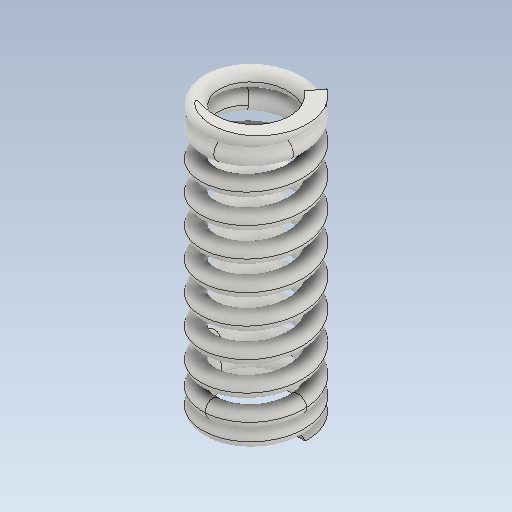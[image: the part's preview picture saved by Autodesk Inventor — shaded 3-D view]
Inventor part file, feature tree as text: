
AUTODESK INVENTOR PART (.ipt)
format: ipt  version: 2020 (Build 240168000, 168)  size: 1,127,424 bytes
history: native  units: mm
features: other x67, extrude x8, helix x5, sketch x3, sweep x2, plane x1
ambient origin geometry x8: Origin, YZ Plane, XZ Plane, XY Plane, X Axis, Y Axis, Z Axis, Center Point
bodies: Solid1 (feature_tree)
feature tree (86):
  other  "Main Coil Path(Right)"
  other  "Section Work Plane(Right)"
  other  "Start Work Plane(Right)"
  other  "End Work Plane(Right)"
  other  "End Cut Work Plane(Right)"
  other  "Start Cut Work Plane(Right)"
  other  "Plain Ends Cut Work Plane 1(Right)"
  other  "Plain Ends Cut Work Plane 2(Right)"
  sweep  "Main Coil Feature(R)"
  other  "Start Transition Coil 1(Right)"
  helix  "Coil  Start Transition 2(R)"  [1 undecoded]
  helix  "Coil  Start Transition 3(R)"  [1 undecoded]
  helix  "Coil  Start Transition 4(R)"  [1 undecoded]
  other  "Start Ends Coil(Right)"
  extrude  "Start Cut Feature(Right)"  Depth=10.0mm
  other  "End Transition Coil 1(Right)"
  other  "End Transition Coil 2(Right)"
  other  "End Transition Coil 3(Right)"
  other  "End Transition Coil 4(Right)"
  other  "End Coil(Right)"
  extrude  "End Cut Feature(Right)"  Depth=10.0mm
  extrude  "Plain Ends Cut Feature 1(Right)"  Depth=10.0mm
  extrude  "Plain Ends Cut  2(R)"  Depth=10.0mm TaperAngle=0.0deg
  other  "Main Coil Path(Left)"
  other  "Section Work Plane(Left)"
  other  "Start Work Plane(Left)"
  other  "End Work Plane(Left)"
  other  "End Cut Work Plane(Left)"
  other  "Start Cut Work Plane(Left)"
  other  "Plain Ends Cut Work Plane 1(Left)"
  other  "Plain Ends Cut Work Plane 2(Left)"
  sweep  "Main Coil Feature(L)"
  other  "Start Transition Coil 1(Left)"
  other  "Start Transition Coil 2(Left)"
  other  "Start Transition Coil 3(Left)"
  other  "Start Transition Coil 4(Left)"
  other  "Start Ends Coil(Left)"
  extrude  "Start Cut Feature(Left)"  Depth=10.0mm TaperAngle=0.0deg
  other  "End Transition Coil 1(Left)"
  other  "End Transition Coil 2(Left)"
  other  "End Transition Coil 3(Left)"
  other  "End Transition Coil 4(Left)"
  other  "End Coil(Left)"
  extrude  "End Cut Feature(Left)"  Depth=10.0mm
  extrude  "Cut Plain Ends Cut 1(L)"  TaperAngle=0.0deg  [1 undecoded]
  extrude  "Cut Plain Ends Cut 2(L)"  TaperAngle=0.0deg  [1 undecoded]
  other  "iMate Based Work Plane"
  other  "Preview Center Point"
  other  "Preview X Axis"
  other  "Path Section Sketch(Right)"
  other  "Srf1"
  helix  "Coil Section Sketch(Right)"  [1 undecoded]
  other  "Start Transition Coil Sketch 1(Right)"
  sketch  "Sketch  Start Transition 2(R)"  dims[d0=0.3mm d2=2.11556mm d3=10.0mm d4=69.0mm]
  sketch  "Sketch  Start Transition 3(R)"  dims[d5=0.0mm d6=90.0deg d7=90.0deg d8=0.0mm d9=0.0mm d12=2.357522mm d13=-3.04512mm d14=1.2mm]
  sketch  "Sketch  Start Transition 4(R)"  dims[d15=0.0mm d16=1.88667mm d17=10.0mm d18=2.5mm d19=0.0mm d20=90.0deg d21=90.0deg d22=0.0mm d23=0.0mm d24=1.65778mm d25=10.0mm d26=2.5mm d27=0.0mm d28=90.0deg d29=90.0deg d30=0.0mm d31=0.0mm d32=1.42889mm d33=10.0mm d34=2.5mm d35=0.0mm d36=90.0deg d37=90.0deg d38=0.0mm d39=0.0mm d40=1.2mm d41=10.0mm d42=2.5mm d43=0.0mm d44=90.0deg d45=90.0deg d46=0.0mm d47=0.0mm d48=1.88667mm d49=10.0mm d50=1.875mm d51=0.0mm d52=90.0deg d53=90.0deg d54=0.0mm d55=0.0mm d56=1.65778mm d57=10.0mm d58=1.875mm d59=0.0mm d60=90.0deg d61=90.0deg d62=0.0mm d63=0.0mm d64=1.42889mm d65=10.0mm d66=1.875mm d67=0.0mm d68=90.0deg d69=90.0deg d70=0.0mm d71=0.0mm d72=1.2mm d73=10.0mm d74=1.875mm d75=0.0mm d76=90.0deg d77=90.0deg d78=0.0mm d79=0.0mm d81=10.0mm d82=15.0mm d83=0.0mm d84=90.0deg d85=90.0deg d86=0.0mm d87=0.0mm d88=1.207057mm d89=10.0mm d90=10.0mm d91=0.0mm d92=90.0deg d93=90.0deg d94=0.0mm d95=0.0mm d96=7.4mm d97=1.207057mm d98=0.0mm d99=7.4mm d100=1.207057mm d101=0.0mm d102=0.0mm d103=0.0mm d104=0.0mm d105=0.0mm d106=0.0mm d108=0.0mm d112=0.0mm d113=0.0mm d114=0.0mm d121=0.308801mm d131=0.0mm d132=0.0mm d133=0.0mm d134=0.0mm d135=0.3mm d137=2.11556mm d138=10.0mm d139=69.0mm d140=0.0mm d141=90.0deg d142=90.0deg d143=0.0mm d144=0.0mm d145=2.357522mm d146=-3.04512mm d147=0.308801mm d148=0.007037mm d149=1.2mm d150=0.0mm d151=0.0mm d152=1.88667mm d153=10.0mm d154=2.5mm d155=0.0mm d156=90.0deg d157=90.0deg d158=0.0mm d159=0.0mm d160=1.65778mm d161=10.0mm d162=2.5mm d163=0.0mm d164=90.0deg d165=90.0deg d166=0.0mm d167=0.0mm d168=1.42889mm d169=10.0mm d170=2.5mm d171=0.0mm d172=90.0deg d173=90.0deg d174=0.0mm d175=0.0mm d176=1.2mm d177=10.0mm d178=2.5mm d179=0.0mm d180=90.0deg d181=90.0deg d182=0.0mm d183=0.0mm d184=10.0mm d185=10.0mm d186=10.0mm d187=10.0mm d188=1.207057mm d189=10.0mm d190=15.0mm d191=0.0mm d192=90.0deg d193=90.0deg d194=0.0mm d195=0.0mm d196=10.0mm d197=7.4mm d198=1.207057mm d199=0.0mm d200=10.0mm d201=1.88667mm d202=10.0mm d203=1.875mm d204=0.0mm d205=90.0deg d206=90.0deg d207=0.0mm d208=0.0mm d209=10.0mm d210=1.65778mm d211=10.0mm d212=1.875mm d213=0.0mm d214=90.0deg d215=90.0deg d216=0.0mm d217=0.0mm d218=1.42889mm d219=10.0mm d220=1.875mm d221=0.0mm d222=90.0deg d223=90.0deg d224=0.0mm d225=0.0mm d226=1.2mm d227=10.0mm d228=1.875mm d229=0.0mm d230=90.0deg d231=90.0deg d232=0.0mm d233=0.0mm d234=10.0mm d235=10.0mm d236=10.0mm d237=1.207057mm d238=10.0mm d239=10.0mm d240=0.0mm d241=90.0deg d242=90.0deg d243=0.0mm d244=0.0mm d245=7.4mm d246=1.207057mm d247=0.0mm d248=10.0mm d249=10.0mm d254=7.4mm d255=10.0mm d256=0.0mm d257=20.0mm d258=-0.007037mm d259=7.4mm d260=10.0mm d261=0.0mm d262=10.0mm d263=7.4mm d264=10.0mm d265=0.0mm d266=10.0mm d267=0.0mm d270=-2.89512mm d271=0.0mm d272=7.4mm d273=10.0mm d274=0.0mm d275=20.0mm d276=-157.079633mm d277=6.2mm d278=6.2mm d279=0.0mm d280=0.0mm]
  other  "End Transition Coil Sketch 1(Right)"
  other  "End Transition Coil Sketch 2(Right)"
  other  "End Transition Coil Sketch 3(Right)"
  other  "End Transition Coil Sketch 4(Right)"
  other  "Start Ends Skecth(Right)"
  other  "End Coil Skecth(Right)"
  other  "End Cut Sketch(Right)"
  other  "Start Cut Sketch(Right)"
  other  "Path Section Sketch(Left)"
  other  "Srf2"
  helix  "Coil Section Sketch(Left)"  [1 undecoded]
  other  "Start Transition Coil Sketch 1(Left)"
  other  "Start Transition Coil Sketch 2(Left)"
  other  "Start Transition Coil Sketch 3(Left)"
  other  "Start Transition Coil Sketch 4(Left)"
  other  "Start Ends Skecth(Left)"
  other  "Start Cut Sketch(Left)"
  other  "End Transition Coil Sketch 1(Left)"
  other  "End Transition Coil Sketch 2(Left)"
  other  "End Transition Coil Sketch 3(Left)"
  other  "End Transition Coil Sketch 4(Left)"
  other  "End Coil Skecth(Left)"
  other  "End Cut Sketch(Left)"
  other  "Plain Ends Cut Sketch 2(Left)"
  other  "Plain Ends Cut Sketch 2(Right)"
  other  "Plain Ends Cut Sketch 1(Right)"
  other  "Plain Ends Cut Sketch 1(Left)"
  plane  "Work Plane Start Section"
  other  "Basic Curve(Right)"
  other  "Basic Curve(Left)"
note: 7 required parameter values undecoded (feature->parameter linkage not recoverable at this tier; creation-order binding heuristic only, values carry confidence <= 0.55)
